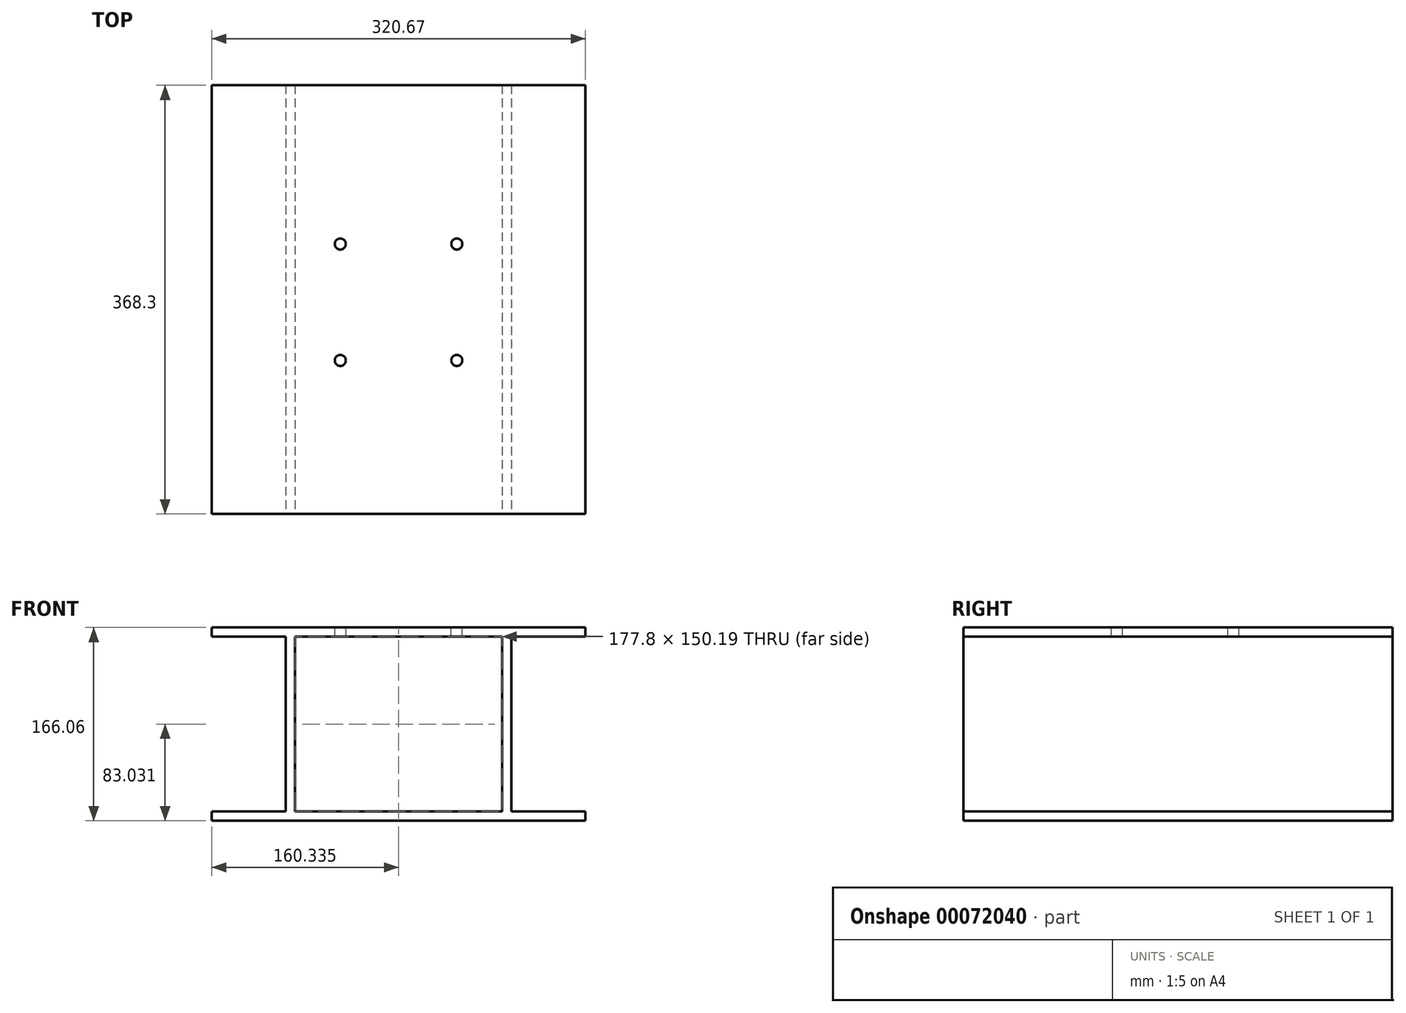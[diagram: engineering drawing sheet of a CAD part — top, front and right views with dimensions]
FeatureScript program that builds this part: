
annotation { "Feature Type Name" : "Feature", "Feature Type Description" : "" }
export const myFeature = defineFeature(function(context is Context, id is Id, definition is map)
    precondition{}
    {
        {
            var Q0;
            Q0=qCreatedBy(makeId("Top.planeOp"),FACE);
            var sketch = newSketch(context, id + "F0", { "sketchPlane" : qUnion([Q0])});
            skLineSegment(sketch, "E0.bottom", {"start": v(-161.06, 205.75) * mm, "end": v(159.61, 205.75) * mm});
            skLineSegment(sketch, "E0.top", {"start": v(-161.06, -162.55) * mm, "end": v(159.61, -162.55) * mm});
            skLineSegment(sketch, "E0.left", {"start": v(-161.06, 205.75) * mm, "end": v(-161.06, -162.55) * mm});
            skLineSegment(sketch, "E0.right", {"start": v(159.61, 205.75) * mm, "end": v(159.61, -162.55) * mm});
            skSolve(sketch);
        }
        {
            var Q0;
            Q0 = qSketchRegion(id + "F0", true);
            extrude(context, id + "F1", {"entities" : qUnion([Q0]), "depth" : 166.06 * mm});
        }
        {
            var Q0;
            Q0=makeQuery(id+"F1.opExtrude","CAP_FACE",FACE,{"disambiguationData":[OSD([sQuery(id+"F0.wireOp",EDGE,"E0.bottom"),sQuery(id+"F0.wireOp",EDGE,"E0.top"),sQuery(id+"F0.wireOp",EDGE,"E0.left"),sQuery(id+"F0.wireOp",EDGE,"E0.right")])],"isStart":false});
            var sketch = newSketch(context, id + "F2", { "sketchPlane" : qUnion([Q0])});
            skLineSegment(sketch, "E1.bottom", {"start": v(-50.72, 69.37) * mm, "end": v(49.28, 69.37) * mm});
            skLineSegment(sketch, "E1.top", {"start": v(-50.72, -30.63) * mm, "end": v(49.28, -30.63) * mm});
            skLineSegment(sketch, "E1.left", {"start": v(-50.72, 69.37) * mm, "end": v(-50.72, -30.63) * mm});
            skLineSegment(sketch, "E1.right", {"start": v(49.28, 69.37) * mm, "end": v(49.28, -30.63) * mm});
            skSolve(sketch);
        }
        {
            var Q0;
            Q0=sQuery(id+"F2.wireOp",VERTEX,"E1.left.start");
            var Q1;
            Q1=sQuery(id+"F2.wireOp",VERTEX,"E1.right.start");
            var Q2;
            Q2=sQuery(id+"F2.wireOp",VERTEX,"E1.top.end");
            var Q3;
            Q3=sQuery(id+"F2.wireOp",VERTEX,"E1.left.end");
            var Q4;
            Q4=makeQuery(id+"F1.opExtrude","SWEPT_BODY",BODY,{"disambiguationData":[OSD([sQuery(id+"F0.wireOp",EDGE,"E0.bottom"),sQuery(id+"F0.wireOp",EDGE,"E0.top"),sQuery(id+"F0.wireOp",EDGE,"E0.left"),sQuery(id+"F0.wireOp",EDGE,"E0.right")])]});
            hole(context, id + "F3", {"style" : HoleStyle.SIMPLE, "holeDiameter" : 9.52 * mm, "endStyle" : HoleEndStyle.BLIND, "holeDepth" : 38.1 * mm, "locations" : qUnion([Q0, Q1, Q2, Q3]), "scope" : qUnion([Q4])});
        }
        {
            var Q0;
            Q0=makeQuery(id+"F1.opExtrude","SWEPT_FACE",FACE,{"disambiguationData":[OSD([sQuery(id+"F0.wireOp",EDGE,"E0.top")])]});
            var sketch = newSketch(context, id + "F4", { "sketchPlane" : qUnion([Q0])});
            skLineSegment(sketch, "E2.bottom", {"start": v(-161.06, 158.13) * mm, "end": v(-97.56, 158.13) * mm});
            skLineSegment(sketch, "E2.top", {"start": v(-161.06, 7.94) * mm, "end": v(-97.56, 7.94) * mm});
            skLineSegment(sketch, "E2.left", {"start": v(-161.06, 158.13) * mm, "end": v(-161.06, 7.94) * mm});
            skLineSegment(sketch, "E2.right", {"start": v(-97.56, 158.13) * mm, "end": v(-97.56, 7.94) * mm});
            skLineSegment(sketch, "E3.bottom", {"start": v(159.61, 158.13) * mm, "end": v(96.11, 158.13) * mm});
            skLineSegment(sketch, "E3.top", {"start": v(159.61, 7.94) * mm, "end": v(96.11, 7.94) * mm});
            skLineSegment(sketch, "E3.left", {"start": v(159.61, 158.13) * mm, "end": v(159.61, 7.94) * mm});
            skLineSegment(sketch, "E3.right", {"start": v(96.11, 158.13) * mm, "end": v(96.11, 7.94) * mm});
            skLineSegment(sketch, "E4.bottom", {"start": v(-89.62, 158.13) * mm, "end": v(88.18, 158.13) * mm});
            skLineSegment(sketch, "E4.top", {"start": v(-89.62, 7.94) * mm, "end": v(88.18, 7.94) * mm});
            skLineSegment(sketch, "E4.left", {"start": v(-89.62, 158.13) * mm, "end": v(-89.62, 7.94) * mm});
            skLineSegment(sketch, "E4.right", {"start": v(88.18, 158.13) * mm, "end": v(88.18, 7.94) * mm});
            skSolve(sketch);
        }
        {
            var Q0;
            Q0 = qSketchRegion(id + "F4", true);
            extrude(context, id + "F5", {"entities" : qUnion([Q0]), "operationType" : NewBodyOperationType.REMOVE, "endBound" : BoundingType.THROUGH_ALL, "oppositeDirection" : true, "depth" : 25.4 * mm});
        }
    });
